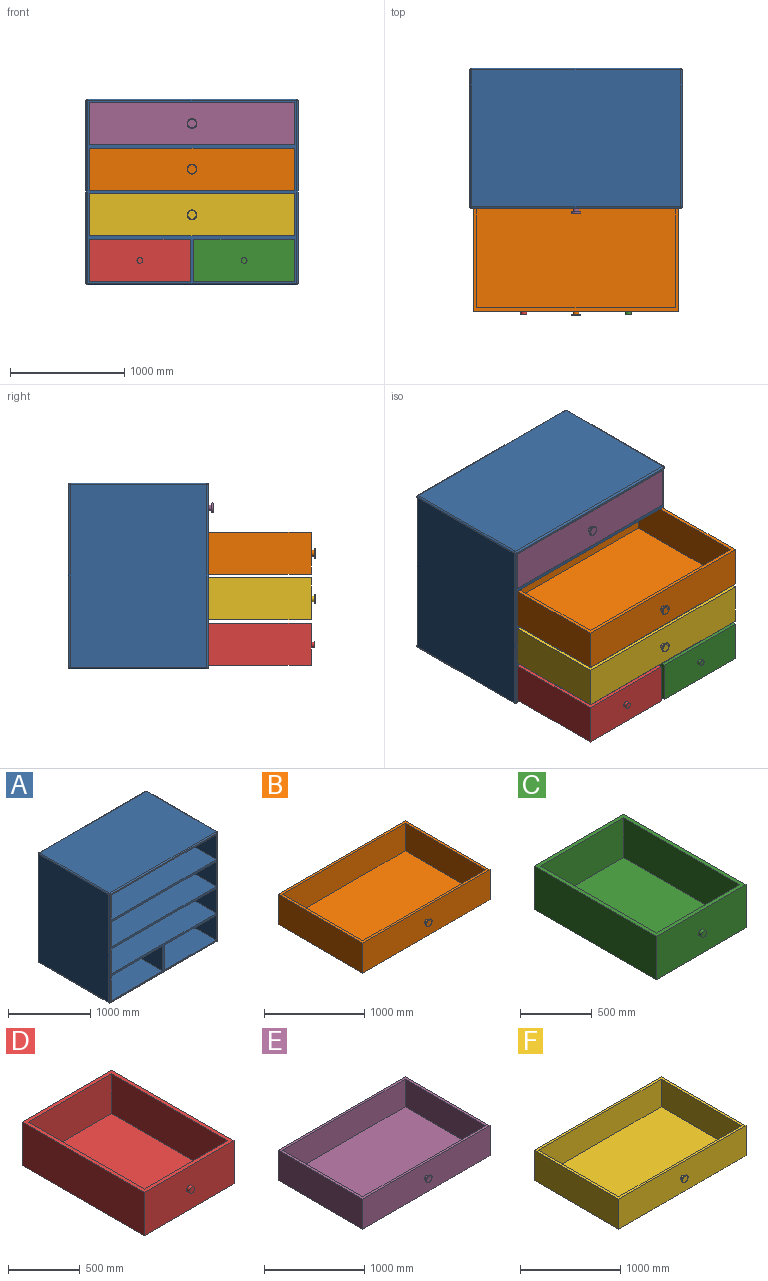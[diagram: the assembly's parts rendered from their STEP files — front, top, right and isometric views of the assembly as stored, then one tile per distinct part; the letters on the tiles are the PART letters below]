
ASSEMBLY  parts=6 mates=5
PART A: 51 faces, bbox 1860x1230x1630 mm
  f0: plane 885x370mm, normal (0,-1,0), area 327450mm2, adj f15,f21,f28,f29
  f1: plane 1200x885mm, normal (0,0,1), area 1062000mm2, adj f3,f12,f20,f30
  f2: plane 1200x885mm, normal (0,0,-1), area 1062000mm2, adj f3,f12,f20,f30
  f3: plane 1200x370mm, normal (-1,0,0), area 444000mm2, adj f1,f2,f12,f20
  f4: plane 1200x370mm, normal (1,0,0), area 444000mm2, adj f5,f12,f23,f27
  f5: plane 1800x370mm, normal (0,-1,0), area 666000mm2, adj f4,f10,f23,f27
  f6: plane 1200x370mm, normal (1,0,0), area 444000mm2, adj f7,f12,f14,f25
  f7: plane 1800x370mm, normal (0,-1,0), area 666000mm2, adj f6,f14,f17,f25
  f8: plane 1200x370mm, normal (-1,0,0), area 444000mm2, adj f11,f12,f24,f26
  f9: plane 1200x370mm, normal (1,0,0), area 444000mm2, adj f11,f12,f24,f26
  f10: plane 1200x370mm, normal (-1,0,0), area 444000mm2, adj f5,f12,f23,f27
  f11: plane 1800x370mm, normal (0,-1,0), area 666000mm2, adj f8,f9,f24,f26
  f12: plane 1830x1600mm, normal (0,-1,0), area 275100mm2, adj f1,f2,f3,f4,f6,f8,f9,f10
  f13: plane 1830x1200mm, normal (0,0,1), area 2196000mm2, adj f31,f35,f36,f37
  f14: plane 1800x1200mm, normal (0,0,-1), area 2160000mm2, adj f6,f7,f12,f17
  f15: plane 1200x370mm, normal (1,0,0), area 444000mm2, adj f0,f12,f21,f28
  f16: plane 1600x1200mm, normal (-1,0,0), area 1920000mm2, adj f37,f38,f46,f47
  f17: plane 1200x370mm, normal (-1,0,0), area 444000mm2, adj f7,f12,f14,f25
  f18: plane 1600x1200mm, normal (1,0,0), area 1920000mm2, adj f34,f35,f44,f45
  f19: plane 1830x1600mm, normal (0,1,0), area 2928000mm2, adj f36,f45,f46,f50
  f20: plane 885x370mm, normal (0,-1,0), area 327450mm2, adj f1,f2,f3,f30
  f21: plane 1200x885mm, normal (0,0,1), area 1062000mm2, adj f0,f12,f15,f29
  f22: plane 1830x1200mm, normal (0,0,-1), area 2196000mm2, adj f39,f44,f47,f50
  f23: plane 1800x1200mm, normal (0,0,-1), area 2160000mm2, adj f4,f5,f10,f12
  f24: plane 1800x1200mm, normal (0,0,1), area 2160000mm2, adj f8,f9,f11,f12
  f25: plane 1800x1200mm, normal (0,0,1), area 2160000mm2, adj f6,f7,f12,f17
  f26: plane 1800x1200mm, normal (0,0,-1), area 2160000mm2, adj f8,f9,f11,f12
  f27: plane 1800x1200mm, normal (0,0,1), area 2160000mm2, adj f4,f5,f10,f12
  f28: plane 1200x885mm, normal (0,0,-1), area 1062000mm2, adj f0,f12,f15,f29
  f29: plane 1200x370mm, normal (-1,0,0), area 444000mm2, adj f0,f12,f21,f28
  f30: plane 1200x370mm, normal (1,0,0), area 444000mm2, adj f1,f2,f12,f20
  f31: cylinder r=15mm len=1830mm, axis (-1,0,0), area 43118.4mm2, adj f12,f13,f32,f33
  f32: sphere r=15mm, area 353.4mm2, adj f31,f34,f35
  f33: sphere r=15mm, area 353.4mm2, adj f31,f37,f38
  f34: cylinder r=15mm len=1600mm, axis (0,0,-1), area 37699.1mm2, adj f12,f18,f32,f40
  f35: cylinder r=15mm len=1200mm, axis (0,-1,0), area 28274.3mm2, adj f13,f18,f32,f41
  f36: cylinder r=15mm len=1830mm, axis (-1,0,0), area 43118.4mm2, adj f13,f19,f41,f42
  f37: cylinder r=15mm len=1200mm, axis (0,-1,0), area 28274.3mm2, adj f13,f16,f33,f42
  f38: cylinder r=15mm len=1600mm, axis (0,0,-1), area 37699.1mm2, adj f12,f16,f33,f43
  f39: cylinder r=15mm len=1830mm, axis (1,0,0), area 43118.4mm2, adj f12,f22,f40,f43
  f40: sphere r=15mm, area 353.4mm2, adj f34,f39,f44
  f41: sphere r=15mm, area 353.4mm2, adj f35,f36,f45
  f42: sphere r=15mm, area 353.4mm2, adj f36,f37,f46
  f43: sphere r=15mm, area 353.4mm2, adj f38,f39,f47
  f44: cylinder r=15mm len=1200mm, axis (0,-1,0), area 28274.3mm2, adj f18,f22,f40,f48
  f45: cylinder r=15mm len=1600mm, axis (0,0,-1), area 37699.1mm2, adj f18,f19,f41,f48
  f46: cylinder r=15mm len=1600mm, axis (0,0,-1), area 37699.1mm2, adj f16,f19,f42,f49
  f47: cylinder r=15mm len=1200mm, axis (0,-1,0), area 28274.3mm2, adj f16,f22,f43,f49
  f48: sphere r=15mm, area 353.4mm2, adj f44,f45,f50
  f49: sphere r=15mm, area 353.4mm2, adj f46,f47,f50
  f50: cylinder r=15mm len=1830mm, axis (-1,0,0), area 43118.4mm2, adj f19,f22,f48,f49
PART B: 15 faces, bbox 1798x1240x368 mm
  f0: plane 1738x1140mm, normal (0,0,1), area 1981320mm2, adj f1,f2,f3,f10
  f1: plane 1140x338mm, normal (1,0,0), area 385320mm2, adj f0,f3,f5,f10
  f2: plane 1140x338mm, normal (-1,0,0), area 385320mm2, adj f0,f3,f5,f10
  f3: plane 1738x338mm, normal (0,-1,0), area 587444mm2, adj f0,f1,f2,f5
  f4: plane 1200x368mm, normal (1,0,0), area 441600mm2, adj f5,f7,f8,f9
  f5: plane 1798x1200mm, normal (0,0,1), area 176280mm2, adj f1,f2,f3,f4,f6,f8,f9,f10
  f6: plane 1200x368mm, normal (-1,0,0), area 441600mm2, adj f5,f7,f8,f9
  f7: plane 1798x1200mm, normal (0,0,-1), area 2157600mm2, adj f4,f6,f8,f9
  f8: plane 1798x368mm, normal (0,1,0), area 661664mm2, adj f4,f5,f6,f7
  f9: plane 1798x368mm, normal (0,-1,0), area 659700.5mm2, adj f4,f5,f6,f7,f11
  f10: plane 1738x338mm, normal (0,1,0), area 587444mm2, adj f0,f1,f2,f5
  f11: cylinder r=25mm len=50mm, axis (0,1,0), area 4712.4mm2, adj f9,f13
  f12: plane 75.11x75.11mm, normal (0,-1,0), area 4431.2mm2, adj f14
  f13: plane 75.11x75.11mm, normal (0,1,0), area 2467.7mm2, adj f11,f14
  f14: torus R=37.56mm, axis (0,-1,0), area 4020.8mm2, adj f12,f13
PART C: 13 faces, bbox 883x1230x368 mm
  f0: plane 1140x823mm, normal (0,0,1), area 938220mm2, adj f1,f8,f9,f10
  f1: plane 1140x338mm, normal (-1,0,0), area 385320mm2, adj f0,f7,f8,f10
  f2: plane 883x368mm, normal (0,-1,0), area 322980.5mm2, adj f3,f5,f6,f7,f11
  f3: plane 1200x368mm, normal (-1,0,0), area 441600mm2, adj f2,f4,f6,f7
  f4: plane 883x368mm, normal (0,1,0), area 324944mm2, adj f3,f5,f6,f7
  f5: plane 1200x368mm, normal (1,0,0), area 441600mm2, adj f2,f4,f6,f7
  f6: plane 1200x883mm, normal (0,0,-1), area 1059600mm2, adj f2,f3,f4,f5
  f7: plane 1200x883mm, normal (0,0,1), area 121380mm2, adj f1,f2,f3,f4,f5,f8,f9,f10
  f8: plane 823x338mm, normal (0,-1,0), area 278174mm2, adj f0,f1,f7,f9
  f9: plane 1140x338mm, normal (1,0,0), area 385320mm2, adj f0,f7,f8,f10
  f10: plane 823x338mm, normal (0,1,0), area 278174mm2, adj f0,f1,f7,f9
  f11: cylinder r=25mm len=50mm, axis (0,1,0), area 4712.4mm2, adj f2,f12
  f12: plane 50x50mm, normal (0,-1,0), area 1963.5mm2, adj f11
PART D: 13 faces, bbox 883x1230x368 mm
  f0: plane 1140x823mm, normal (0,0,1), area 938220mm2, adj f1,f8,f9,f10
  f1: plane 1140x338mm, normal (1,0,0), area 385320mm2, adj f0,f7,f8,f10
  f2: plane 883x368mm, normal (0,-1,0), area 322980.5mm2, adj f3,f5,f6,f7,f11
  f3: plane 1200x368mm, normal (1,0,0), area 441600mm2, adj f2,f4,f6,f7
  f4: plane 883x368mm, normal (0,1,0), area 324944mm2, adj f3,f5,f6,f7
  f5: plane 1200x368mm, normal (-1,0,0), area 441600mm2, adj f2,f4,f6,f7
  f6: plane 1200x883mm, normal (0,0,-1), area 1059600mm2, adj f2,f3,f4,f5
  f7: plane 1200x883mm, normal (0,0,1), area 121380mm2, adj f1,f2,f3,f4,f5,f8,f9,f10
  f8: plane 823x338mm, normal (0,-1,0), area 278174mm2, adj f0,f1,f7,f9
  f9: plane 1140x338mm, normal (-1,0,0), area 385320mm2, adj f0,f7,f8,f10
  f10: plane 823x338mm, normal (0,1,0), area 278174mm2, adj f0,f1,f7,f9
  f11: cylinder r=25mm len=50mm, axis (0,1,0), area 4712.4mm2, adj f2,f12
  f12: plane 50x50mm, normal (0,-1,0), area 1963.5mm2, adj f11
PART E: 15 faces, bbox 1798x1240x368 mm
  f0: plane 1738x1140mm, normal (0,0,1), area 1981320mm2, adj f1,f2,f3,f10
  f1: plane 1140x338mm, normal (1,0,0), area 385320mm2, adj f0,f3,f5,f10
  f2: plane 1140x338mm, normal (-1,0,0), area 385320mm2, adj f0,f3,f5,f10
  f3: plane 1738x338mm, normal (0,-1,0), area 587444mm2, adj f0,f1,f2,f5
  f4: plane 1200x368mm, normal (1,0,0), area 441600mm2, adj f5,f7,f8,f9
  f5: plane 1798x1200mm, normal (0,0,1), area 176280mm2, adj f1,f2,f3,f4,f6,f8,f9,f10
  f6: plane 1200x368mm, normal (-1,0,0), area 441600mm2, adj f5,f7,f8,f9
  f7: plane 1798x1200mm, normal (0,0,-1), area 2157600mm2, adj f4,f6,f8,f9
  f8: plane 1798x368mm, normal (0,1,0), area 661664mm2, adj f4,f5,f6,f7
  f9: plane 1798x368mm, normal (0,-1,0), area 659700.5mm2, adj f4,f5,f6,f7,f11
  f10: plane 1738x338mm, normal (0,1,0), area 587444mm2, adj f0,f1,f2,f5
  f11: cylinder r=25mm len=50mm, axis (0,1,0), area 4712.4mm2, adj f9,f13
  f12: plane 75.11x75.11mm, normal (0,-1,0), area 4431.2mm2, adj f14
  f13: plane 75.11x75.11mm, normal (0,1,0), area 2467.7mm2, adj f11,f14
  f14: torus R=37.56mm, axis (0,-1,0), area 4020.8mm2, adj f12,f13
PART F: 15 faces, bbox 1798x1240x368 mm
  f0: plane 1738x1140mm, normal (0,0,1), area 1981320mm2, adj f1,f2,f3,f10
  f1: plane 1140x338mm, normal (1,0,0), area 385320mm2, adj f0,f3,f5,f10
  f2: plane 1140x338mm, normal (-1,0,0), area 385320mm2, adj f0,f3,f5,f10
  f3: plane 1738x338mm, normal (0,-1,0), area 587444mm2, adj f0,f1,f2,f5
  f4: plane 1200x368mm, normal (1,0,0), area 441600mm2, adj f5,f7,f8,f9
  f5: plane 1798x1200mm, normal (0,0,1), area 176280mm2, adj f1,f2,f3,f4,f6,f8,f9,f10
  f6: plane 1200x368mm, normal (-1,0,0), area 441600mm2, adj f5,f7,f8,f9
  f7: plane 1798x1200mm, normal (0,0,-1), area 2157600mm2, adj f4,f6,f8,f9
  f8: plane 1798x368mm, normal (0,1,0), area 661664mm2, adj f4,f5,f6,f7
  f9: plane 1798x368mm, normal (0,-1,0), area 659700.5mm2, adj f4,f5,f6,f7,f11
  f10: plane 1738x338mm, normal (0,1,0), area 587444mm2, adj f0,f1,f2,f5
  f11: cylinder r=25mm len=50mm, axis (0,1,0), area 4712.4mm2, adj f9,f13
  f12: plane 75.11x75.11mm, normal (0,-1,0), area 4431.2mm2, adj f14
  f13: plane 75.11x75.11mm, normal (0,1,0), area 2467.7mm2, adj f11,f14
  f14: torus R=37.56mm, axis (0,-1,0), area 4020.8mm2, adj f12,f13
PLACE A t=(-578.78,0,418.87)mm fixed
PLACE B t=(-578.78,-900,418.87)mm
PLACE C t=(-578.78,-900,419.87)mm
PLACE D t=(-578.78,-900,419.87)mm
PLACE E t=(-578.78,0,418.87)mm
PLACE F t=(-578.78,-900,418.87)mm
MATE slider A.f0 <-> D.f11  axis (0,-1,0) through (-1036.28,600,-966.13)mm
MATE slider A.f5 <-> F.f11  axis (0,-1,0) through (-578.78,600,-566.13)mm
MATE slider A.f11 <-> B.f11  axis (0,-1,0) through (-578.78,600,-166.13)mm
MATE slider E.f11 <-> A.f7  axis (0,1,0) through (-578.78,600,233.87)mm
MATE slider A.f20 <-> C.f11  axis (0,-1,0) through (-121.28,600,-966.13)mm
